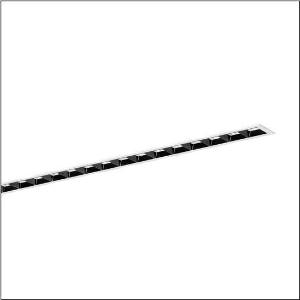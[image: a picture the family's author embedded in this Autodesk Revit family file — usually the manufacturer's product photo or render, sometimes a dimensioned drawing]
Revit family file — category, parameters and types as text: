
# Revit family: silica_r__21_51mx12db45wb_7f54
name_source: partatom
category: Lighting Fixtures
units: mm (PartAtom-declared; Revit-internal decimal feet)

## family parameters
Cut with Voids When Loaded = No
Host = Face
Light Source = No
Part Type = Normal
Room Calculation Point = No
Round Connector Dimension = Use Diameter
Shared = No

## types (1)
- --- (1 x LED, 5400 lm, 32 W, 4000K)
    Apparent Load = 32 VA
    CIE Flux Codes = 86 100 100 100 100
    Color Rendering = 80
    Color Temperature = 4000K
    Default Elevation = 1800 mm
    Description = Silica® 21, office luminaire, primary light control with darklight reflector, of PMMA, black, CAT 2 (L<= 3000cd/m²), light emission: direct distribution, primary light characteristic: symmetric, installation type: recessed, LED, rated luminous flux: 5.400lm, luminous efficacy: 169lm/W, light colour: 840, colour temperature: 4000K, with terminal, 3+2-pole, max. 2.5mm², mains connection: 220..240V, AC, 50/60Hz, rated input power: 32W, luminaire housing, of aluminium, traffic white (RAL 9016), length: 1.528mm, width: 79mm, height: 53mm, protection rating (complete): IP20, insulation class (complete): insulation class I (protective earthing), certification: CE, permissible operating ambient temperature: 0..+35°C, standard: EN 50419, packaging unit: 1 piece
    Height = 0 mm  [stored 0 ft]
    Lamp = 1 x LED
    Lamp Light Flux = 5400 lm
    Lamp Power = 32 W
    Lamp count = 1
    Length = 1527 mm
    Luminous efficacy = 169 lm/W
    Manufacturer = Siteco
    ModVariant = No
    Model = 51MX12DB45WB
    Mounting Place = Ceiling
    Mounting Type = Recessed
    Number of Poles = 1
    OnlyDefault = Yes
    Power Factor = 1
    Product Name = Silica® 21
    Product group = office luminaire | ceiling recessed
    ProductGroupID = 401
    Protection Class = Protection class I
    Protection Degree = IP 20
    RLX_Detail_Level = 1
    RLX_Emergency_Light_Flux = 0 lm
    RLX_Emergency_Type = 0
    RLX_Emergency_Type_DB = No
    RlxData = <blob elided: 42281 chars, md5=d2b91baf>
    Socket = socket
    Standby Power = 0 W
    System Light Flux = 5400 lm
    System Power = 32 W
    Type Comments = factory setting: luminous flux: 100 % | dim-lin: 254 | 366 mA
    Type Image = l_1297791.jpg
    URL = http://relux.com
    VarID = @adj_055661
    Voltage = 0 V
    Weight = 0.00 kg
    Width = 79 mm

note: [stored X ft] marks values corroborated as IEEE doubles in the binary element streams (Revit-internal decimal feet)

## geometry (parser evidence)
native form markers: Blend x4, Sweep x9
no freeform markers — native parametric forms only
